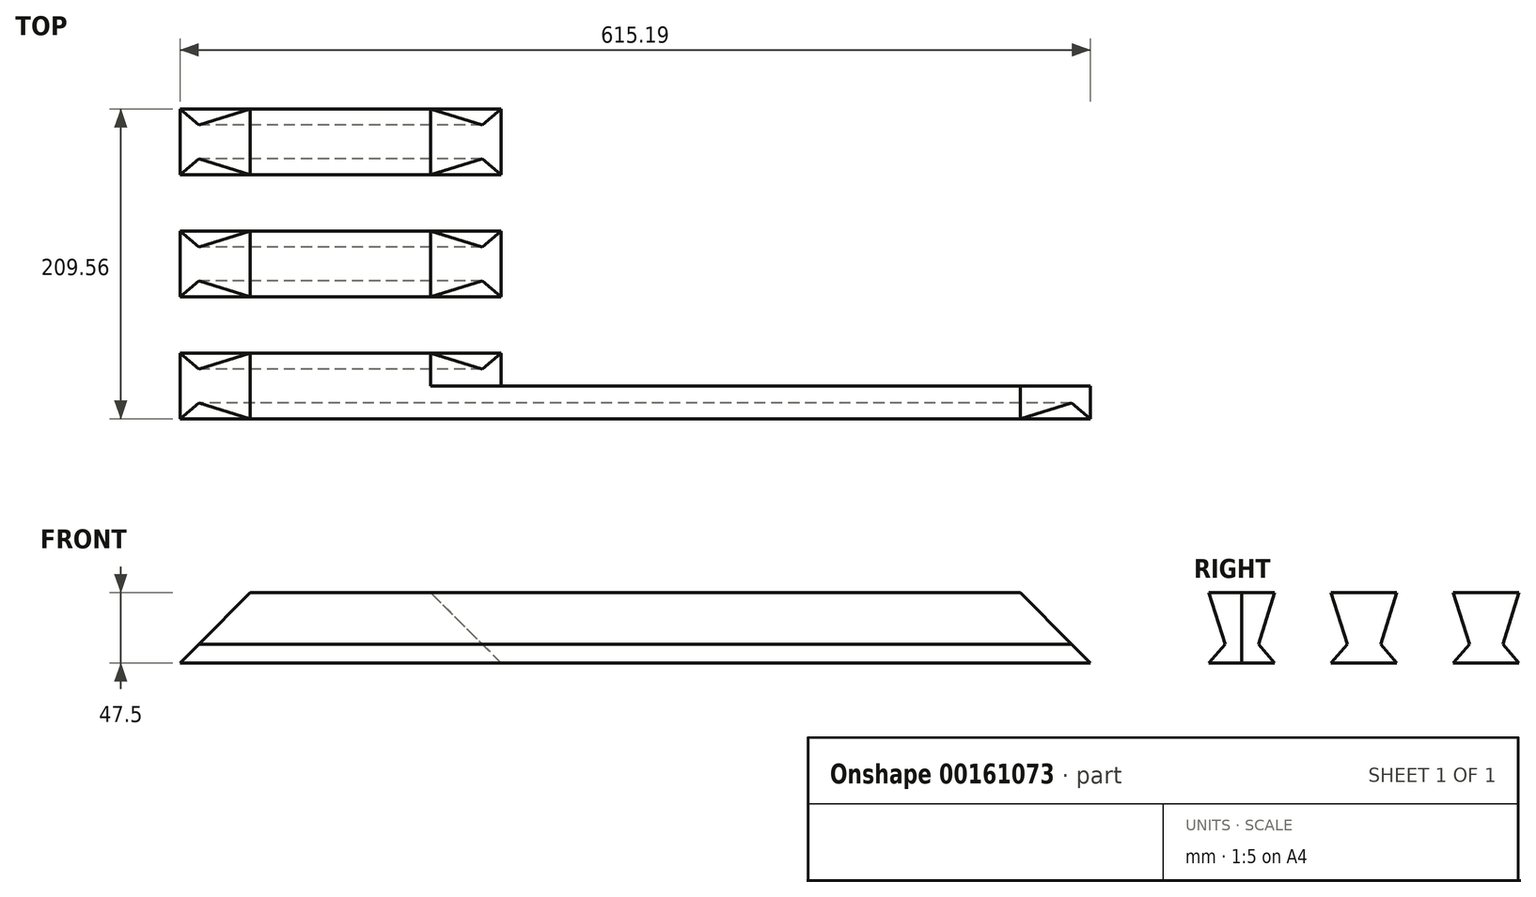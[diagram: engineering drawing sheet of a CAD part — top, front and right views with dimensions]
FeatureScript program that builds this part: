
annotation { "Feature Type Name" : "Feature", "Feature Type Description" : "" }
export const myFeature = defineFeature(function(context is Context, id is Id, definition is map)
    precondition{}
    {
        {
            var Q0;
            Q0=qCreatedBy(makeId("Right.planeOp"),FACE);
            var sketch = newSketch(context, id + "F0", { "sketchPlane" : qUnion([Q0])});
            skLineSegment(sketch, "E0", {"start": v(0, 0) * mm, "end": v(-22.23, 0) * mm});
            skLineSegment(sketch, "E1", {"start": v(-22.23, 0) * mm, "end": v(-11.3, 12.7) * mm});
            skLineSegment(sketch, "E2", {"start": v(-11.3, 12.7) * mm, "end": v(-22.23, 47.5) * mm});
            skLineSegment(sketch, "E3", {"start": v(-22.23, 47.5) * mm, "end": v(22.22, 47.5) * mm});
            skLineSegment(sketch, "E4", {"start": v(22.22, 47.5) * mm, "end": v(11.3, 12.7) * mm});
            skLineSegment(sketch, "E5", {"start": v(11.3, 12.7) * mm, "end": v(22.23, 0) * mm});
            skLineSegment(sketch, "E6", {"start": v(22.23, 0) * mm, "end": v(0, 0) * mm});
            skLineSegment(sketch, "E7.1.0.0", {"start": v(60.32, 47.5) * mm, "end": v(104.77, 47.5) * mm});
            skLineSegment(sketch, "E7.1.0.1", {"start": v(71.25, 12.7) * mm, "end": v(60.32, 47.5) * mm});
            skLineSegment(sketch, "E7.1.0.2", {"start": v(60.32, 0) * mm, "end": v(71.25, 12.7) * mm});
            skLineSegment(sketch, "E7.1.0.3", {"start": v(82.55, 0) * mm, "end": v(60.32, 0) * mm});
            skLineSegment(sketch, "E7.1.0.4", {"start": v(104.78, 0) * mm, "end": v(82.55, 0) * mm});
            skLineSegment(sketch, "E7.1.0.5", {"start": v(93.85, 12.7) * mm, "end": v(104.78, 0) * mm});
            skLineSegment(sketch, "E7.1.0.6", {"start": v(104.77, 47.5) * mm, "end": v(93.85, 12.7) * mm});
            skLineSegment(sketch, "E7.2.0.0", {"start": v(142.88, 47.5) * mm, "end": v(187.32, 47.5) * mm});
            skLineSegment(sketch, "E7.2.0.1", {"start": v(153.8, 12.7) * mm, "end": v(142.88, 47.5) * mm});
            skLineSegment(sketch, "E7.2.0.2", {"start": v(142.88, 0) * mm, "end": v(153.8, 12.7) * mm});
            skLineSegment(sketch, "E7.2.0.3", {"start": v(165.1, 0) * mm, "end": v(142.88, 0) * mm});
            skLineSegment(sketch, "E7.2.0.4", {"start": v(187.32, 0) * mm, "end": v(165.1, 0) * mm});
            skLineSegment(sketch, "E7.2.0.5", {"start": v(176.4, 12.7) * mm, "end": v(187.32, 0) * mm});
            skLineSegment(sketch, "E7.2.0.6", {"start": v(187.33, 47.5) * mm, "end": v(176.4, 12.7) * mm});
            skLineSegment(sketch, "E7.direction1", {"start": v(-22.23, 47.5) * mm, "end": v(60.32, 47.5) * mm, "construction": true});
            skSolve(sketch);
        }
        {
            var Q0;
            Q0 = qSketchRegion(id + "F0", true);
            extrude(context, id + "F1", {"entities" : qUnion([Q0]), "depth" : 615.2 * mm});
        }
        {
            var Q0;
            Q0=qCreatedBy(makeId("Front.planeOp"),FACE);
            var sketch = newSketch(context, id + "F2", { "sketchPlane" : qUnion([Q0])});
            skLineSegment(sketch, "E8", {"start": v(0, 0) * mm, "end": v(50.8, 50.8) * mm});
            skLineSegment(sketch, "E9", {"start": v(50.8, 50.8) * mm, "end": v(0, 50.8) * mm});
            skLineSegment(sketch, "E10", {"start": v(0, 50.8) * mm, "end": v(0, 0) * mm});
            skSolve(sketch);
        }
        {
            var Q0;
            Q0 = qSketchRegion(id + "F2", true);
            extrude(context, id + "F3", {"entities" : qUnion([Q0]), "operationType" : NewBodyOperationType.REMOVE, "endBound" : BoundingType.THROUGH_ALL, "depth" : 25.4 * mm, "hasSecondDirection" : true, "secondDirectionBound" : SecondDirectionBoundingType.THROUGH_ALL, "secondDirectionOppositeDirection" : true, "secondDirectionDepth" : 25.4 * mm});
        }
        {
            var Q0;
            Q0=qCreatedBy(makeId("Front.planeOp"),FACE);
            var sketch = newSketch(context, id + "F4", { "sketchPlane" : qUnion([Q0])});
            skLineSegment(sketch, "E11", {"start": v(615.19, 0) * mm, "end": v(564.39, 50.8) * mm});
            skLineSegment(sketch, "E12", {"start": v(564.39, 50.8) * mm, "end": v(615.19, 50.8) * mm});
            skLineSegment(sketch, "E13", {"start": v(615.19, 50.8) * mm, "end": v(615.19, 0) * mm});
            skSolve(sketch);
        }
        {
            var Q0;
            Q0 = qSketchRegion(id + "F4", true);
            extrude(context, id + "F5", {"entities" : qUnion([Q0]), "operationType" : NewBodyOperationType.REMOVE, "endBound" : BoundingType.THROUGH_ALL, "depth" : 25.4 * mm, "hasSecondDirection" : true, "secondDirectionBound" : SecondDirectionBoundingType.THROUGH_ALL, "secondDirectionOppositeDirection" : true, "secondDirectionDepth" : 25.4 * mm});
        }
        {
            var Q0;
            Q0=qCreatedBy(makeId("Front.planeOp"),FACE);
            var sketch = newSketch(context, id + "F6", { "sketchPlane" : qUnion([Q0])});
            skLineSegment(sketch, "E14", {"start": v(216.92, 0) * mm, "end": v(166.12, 50.8) * mm});
            skLineSegment(sketch, "E15", {"start": v(216.92, 0) * mm, "end": v(667.5, 0) * mm});
            skLineSegment(sketch, "E16", {"start": v(667.5, 0) * mm, "end": v(667.5, 50.8) * mm});
            skLineSegment(sketch, "E17", {"start": v(216.92, 50.8) * mm, "end": v(166.12, 50.8) * mm});
            skLineSegment(sketch, "E18", {"start": v(216.92, 50.8) * mm, "end": v(667.5, 50.8) * mm});
            skLineSegment(sketch, "E19", {"start": v(216.92, 50.8) * mm, "end": v(216.92, 0) * mm});
            skSolve(sketch);
        }
        {
            var Q0;
            Q0 = qSketchRegion(id + "F6", true);
            extrude(context, id + "F7", {"entities" : qUnion([Q0]), "operationType" : NewBodyOperationType.REMOVE, "endBound" : BoundingType.THROUGH_ALL, "oppositeDirection" : true, "depth" : 139.06 * mm});
        }
        {
            var Q0;
            Q0=qCreatedBy(makeId("Front.planeOp"),FACE);
            var sketch = newSketch(context, id + "F8", { "sketchPlane" : qUnion([Q0])});
            skLineSegment(sketch, "E20", {"start": v(303.78, 0) * mm, "end": v(252.98, 50.8) * mm});
            skLineSegment(sketch, "E21", {"start": v(252.98, 50.8) * mm, "end": v(303.78, 50.8) * mm});
            skLineSegment(sketch, "E22", {"start": v(303.78, 50.8) * mm, "end": v(303.78, 0) * mm});
            skLineSegment(sketch, "E23.bottom", {"start": v(303.78, 50.8) * mm, "end": v(739.66, 50.8) * mm});
            skLineSegment(sketch, "E23.top", {"start": v(303.78, 0) * mm, "end": v(739.66, 0) * mm});
            skLineSegment(sketch, "E23.right", {"start": v(739.66, 50.8) * mm, "end": v(739.66, 0) * mm});
            skSolve(sketch);
        }
        {
            var Q0;
            Q0 = qSketchRegion(id + "F8", true);
            extrude(context, id + "F9", {"entities" : qUnion([Q0]), "operationType" : NewBodyOperationType.REMOVE, "endBound" : BoundingType.THROUGH_ALL, "oppositeDirection" : true, "depth" : 25.4 * mm});
        }
    });
